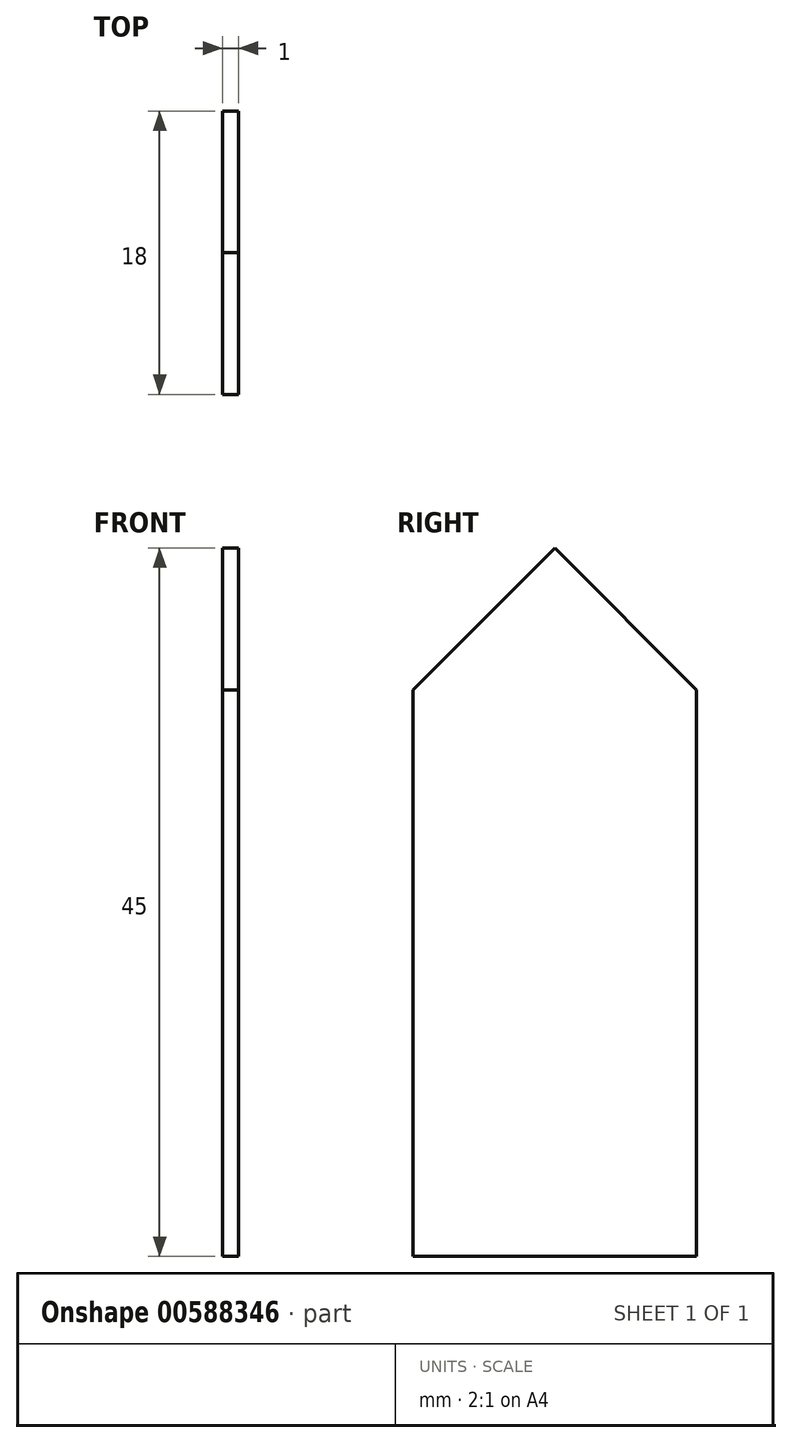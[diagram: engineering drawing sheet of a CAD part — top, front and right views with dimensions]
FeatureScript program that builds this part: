
annotation { "Feature Type Name" : "Feature", "Feature Type Description" : "" }
export const myFeature = defineFeature(function(context is Context, id is Id, definition is map)
    precondition{}
    {
        {
            var Q0;
            Q0=qCreatedBy(makeId("Right.planeOp"),FACE);
            var sketch = newSketch(context, id + "F0", { "sketchPlane" : qUnion([Q0])});
            skLineSegment(sketch, "E0", {"start": v(-39.6, 58.4) * mm, "end": v(-57.6, 40.4) * mm});
            skLineSegment(sketch, "E1", {"start": v(-39.6, 58.4) * mm, "end": v(-21.6, 40.4) * mm});
            skLineSegment(sketch, "E2", {"start": v(-48.6, 13.4) * mm, "end": v(-30.6, 13.4) * mm});
            skLineSegment(sketch, "E3", {"start": v(-43.6, 40.4) * mm, "end": v(-35.6, 40.4) * mm});
            skLineSegment(sketch, "E4", {"start": v(-39.6, 40.4) * mm, "end": v(-35.6, 40.4) * mm});
            skLineSegment(sketch, "E5", {"start": v(-35.6, 40.4) * mm, "end": v(-35.6, 32.4) * mm});
            skLineSegment(sketch, "E6", {"start": v(-43.6, 32.4) * mm, "end": v(-43.6, 40.4) * mm});
            skPoint(sketch, "E7.end.orphan", {"position": v(-39.6, 13.4) * mm});
            skLineSegment(sketch, "E8", {"start": v(-57.6, 40.4) * mm, "end": v(-56.6, 40.4) * mm});
            skLineSegment(sketch, "E9", {"start": v(-56.6, 40.4) * mm, "end": v(-56.6, 15.4) * mm});
            skLineSegment(sketch, "E10", {"start": v(-21.6, 40.4) * mm, "end": v(-22.6, 40.4) * mm});
            skLineSegment(sketch, "E11", {"start": v(-22.6, 40.4) * mm, "end": v(-22.6, 15.4) * mm});
            skPoint(sketch, "E12.orphan", {"position": v(-21.6, 13.4) * mm});
            skPoint(sketch, "E13.orphan", {"position": v(-57.6, 13.4) * mm});
            skLineSegment(sketch, "E14", {"start": v(-57.6, 13.4) * mm, "end": v(-57.6, 15.4) * mm});
            skLineSegment(sketch, "E15", {"start": v(-57.6, 15.4) * mm, "end": v(-56.6, 15.4) * mm});
            skLineSegment(sketch, "E16", {"start": v(-57.6, 13.4) * mm, "end": v(-56.6, 13.4) * mm});
            skLineSegment(sketch, "E17", {"start": v(-21.6, 13.4) * mm, "end": v(-21.6, 15.4) * mm});
            skLineSegment(sketch, "E18", {"start": v(-21.6, 15.4) * mm, "end": v(-22.6, 15.4) * mm});
            skLineSegment(sketch, "E19", {"start": v(-21.6, 13.4) * mm, "end": v(-22.6, 13.4) * mm});
            skLineSegment(sketch, "E20", {"start": v(-30.6, 40.4) * mm, "end": v(-30.6, 49.4) * mm});
            skLineSegment(sketch, "E21", {"start": v(-30.6, 13.4) * mm, "end": v(-30.6, 40.4) * mm});
            skLineSegment(sketch, "E22", {"start": v(-48.6, 40.4) * mm, "end": v(-48.6, 13.4) * mm});
            skLineSegment(sketch, "E23", {"start": v(-48.6, 13.4) * mm, "end": v(-48.6, 40.4) * mm});
            skLineSegment(sketch, "E24", {"start": v(-48.6, 40.4) * mm, "end": v(-48.6, 49.4) * mm});
            skSolve(sketch);
        }
        {
            var Q0;
            Q0=makeQuery(id+"F0.imprint","IMPRINT",FACE,{"disambiguationData":[TD([[makeQuery(id+"F0.imprint","IMPRINT",EDGE,{"derivedFrom":sQuery(id+"F0.wireOp",EDGE,"E2")}),1.0]])]});
            extrude(context, id + "F1", {"entities" : qUnion([Q0]), "depth" : 1 * mm, "offsetDistance" : 25 * mm});
        }
    });
